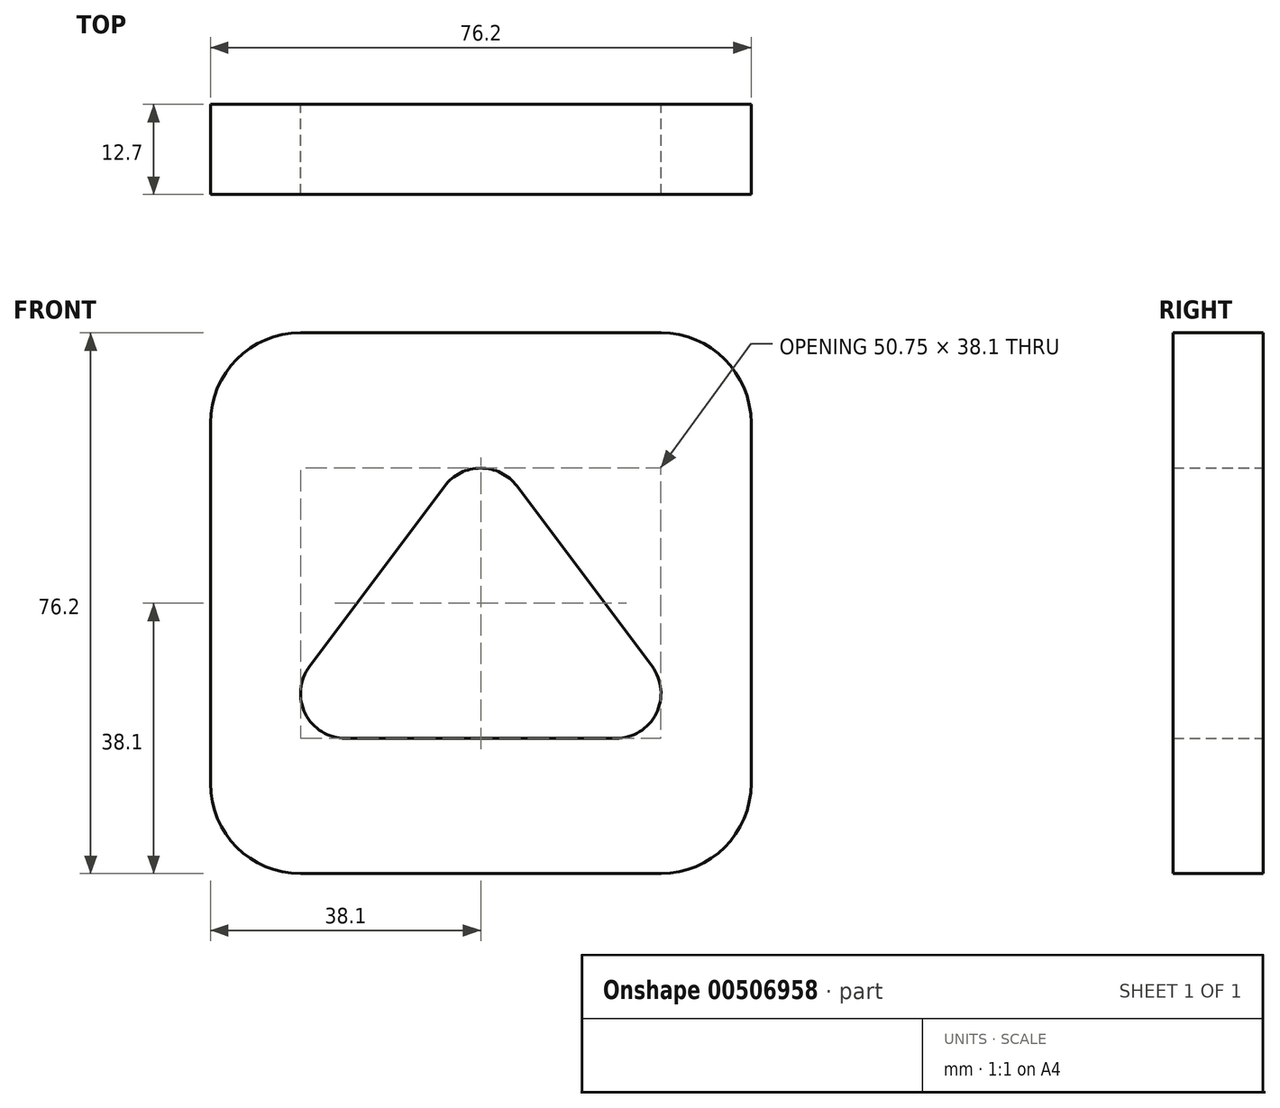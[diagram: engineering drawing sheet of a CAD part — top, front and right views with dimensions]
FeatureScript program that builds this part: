
annotation { "Feature Type Name" : "Feature", "Feature Type Description" : "" }
export const myFeature = defineFeature(function(context is Context, id is Id, definition is map)
    precondition{}
    {
        {
            var Q0;
            Q0=qCreatedBy(makeId("Front.planeOp"),FACE);
            var sketch = newSketch(context, id + "F0", { "sketchPlane" : qUnion([Q0])});
            skLineSegment(sketch, "E0", {"start": v(12.7, 0) * mm, "end": v(63.5, 0) * mm});
            skLineSegment(sketch, "E1", {"start": v(76.2, 12.7) * mm, "end": v(76.2, 63.5) * mm});
            skLineSegment(sketch, "E2", {"start": v(63.5, 76.2) * mm, "end": v(12.7, 76.2) * mm});
            skLineSegment(sketch, "E3", {"start": v(0, 76.2) * mm, "end": v(0, 12.7) * mm});
            skArc(sketch, "E4", {"start": v(43.18, 54.61) * mm, "mid": v(38.1, 57.15) * mm, "end": v(33.02, 54.6) * mm});
            skArc(sketch, "E5", {"start": v(13.97, 29.21) * mm, "mid": v(13.37, 22.56) * mm, "end": v(19.05, 19.05) * mm});
            skArc(sketch, "E6", {"start": v(57.15, 19.05) * mm, "mid": v(62.83, 22.56) * mm, "end": v(62.23, 29.21) * mm});
            skLineSegment(sketch, "E7", {"start": v(33.02, 54.6) * mm, "end": v(13.97, 29.21) * mm});
            skLineSegment(sketch, "E8", {"start": v(19.05, 19.05) * mm, "end": v(57.15, 19.05) * mm});
            skLineSegment(sketch, "E9", {"start": v(62.23, 29.2) * mm, "end": v(43.18, 54.61) * mm});
            skArc(sketch, "E10", {"start": v(12.7, 76.2) * mm, "mid": v(3.72, 72.48) * mm, "end": v(0, 63.5) * mm});
            skArc(sketch, "E11", {"start": v(76.2, 63.5) * mm, "mid": v(72.48, 72.48) * mm, "end": v(63.5, 76.2) * mm});
            skPoint(sketch, "E12.visualSharp", {"position": v(0, 0) * mm});
            skArc(sketch, "E12.filletArc", {"start": v(0, 12.7) * mm, "mid": v(3.72, 3.72) * mm, "end": v(12.7, 0) * mm});
            skPoint(sketch, "E13.visualSharp", {"position": v(76.2, 0) * mm});
            skArc(sketch, "E13.filletArc", {"start": v(63.5, 0) * mm, "mid": v(72.48, 3.72) * mm, "end": v(76.2, 12.7) * mm});
            skSolve(sketch);
        }
        {
            var Q0;
            Q0=makeQuery(id+"F0.imprint","IMPRINT",FACE,{"disambiguationData":[TD([[makeQuery(id+"F0.imprint","IMPRINT",EDGE,{"derivedFrom":sQuery(id+"F0.wireOp",EDGE,"E0")}),1.0]])]});
            extrude(context, id + "F1", {"entities" : qUnion([Q0]), "depth" : 12.7 * mm});
        }
    });
